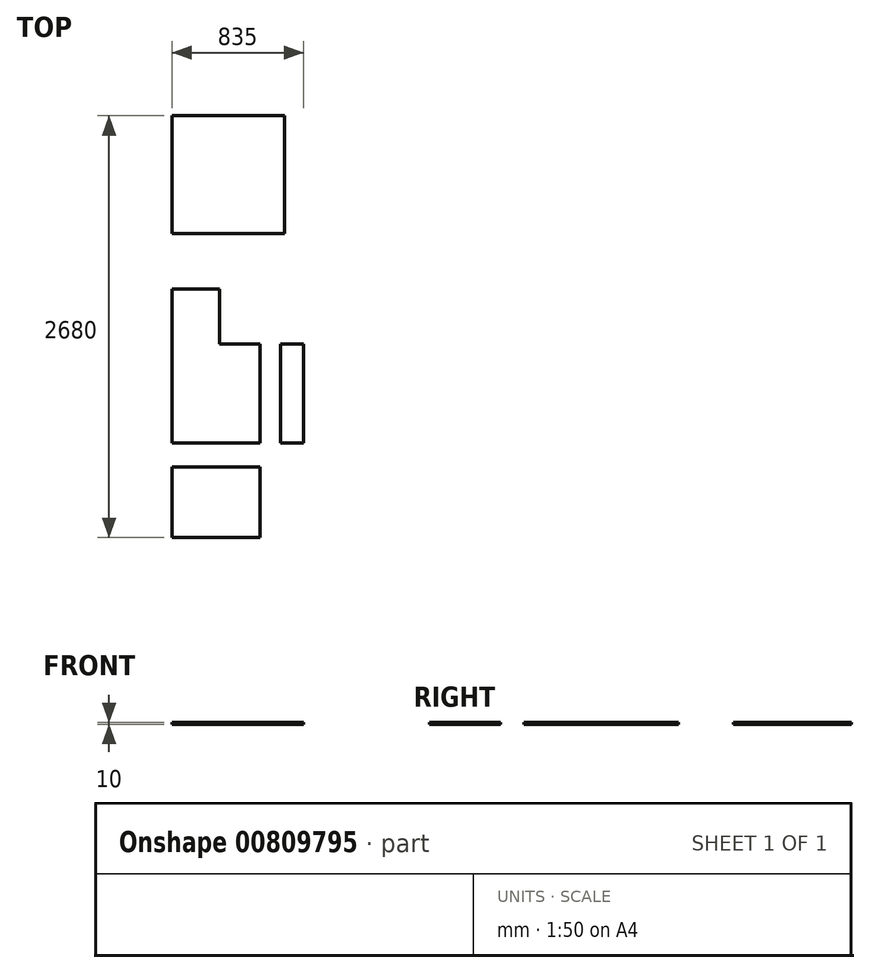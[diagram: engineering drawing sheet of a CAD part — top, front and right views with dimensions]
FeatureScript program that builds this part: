
annotation { "Feature Type Name" : "Feature", "Feature Type Description" : "" }
export const myFeature = defineFeature(function(context is Context, id is Id, definition is map)
    precondition{}
    {
        {
            var Q0;
            Q0=qCreatedBy(makeId("Top.planeOp"),FACE);
            var sketch = newSketch(context, id + "F0", { "sketchPlane" : qUnion([Q0])});
            skLineSegment(sketch, "E0.bottom", {"start": v(0, 0) * mm, "end": v(715, 0) * mm});
            skLineSegment(sketch, "E0.top", {"start": v(0, -750) * mm, "end": v(715, -750) * mm});
            skLineSegment(sketch, "E0.left", {"start": v(0, 0) * mm, "end": v(0, -750) * mm});
            skLineSegment(sketch, "E0.right", {"start": v(715, 0) * mm, "end": v(715, -750) * mm});
            skSolve(sketch);
        }
        {
            var Q0;
            Q0 = qSketchRegion(id + "F0", true);
            extrude(context, id + "F1", {"entities" : qUnion([Q0]), "depth" : 10 * mm, "offsetDistance" : 25 * mm});
        }
        {
            var Q0;
            Q0=qCreatedBy(makeId("Top.planeOp"),FACE);
            var sketch = newSketch(context, id + "F2", { "sketchPlane" : qUnion([Q0])});
            skLineSegment(sketch, "E1.bottom", {"start": v(0, -1100) * mm, "end": v(300, -1100) * mm});
            skLineSegment(sketch, "E1.top", {"start": v(0, -2080) * mm, "end": v(560, -2080) * mm});
            skLineSegment(sketch, "E1.left", {"start": v(0, -1100) * mm, "end": v(0, -2080) * mm});
            skLineSegment(sketch, "E1.right", {"start": v(560, -1450) * mm, "end": v(560, -2080) * mm});
            skLineSegment(sketch, "E2.top", {"start": v(300, -1450) * mm, "end": v(560, -1450) * mm});
            skLineSegment(sketch, "E2.left", {"start": v(300, -1100) * mm, "end": v(300, -1450) * mm});
            skSolve(sketch);
        }
        {
            var Q0;
            Q0=makeQuery(id+"F2.imprint","IMPRINT",FACE,{"disambiguationData":[TD([[makeQuery(id+"F2.imprint","IMPRINT",EDGE,{"derivedFrom":sQuery(id+"F2.wireOp",EDGE,"E1.bottom")}),-1.0]])]});
            extrude(context, id + "F3", {"entities" : qUnion([Q0]), "depth" : 10 * mm, "offsetDistance" : 25 * mm});
        }
        {
            var Q0;
            Q0=qCreatedBy(makeId("Top.planeOp"),FACE);
            var sketch = newSketch(context, id + "F4", { "sketchPlane" : qUnion([Q0])});
            skLineSegment(sketch, "E3.bottom", {"start": v(690, -1450) * mm, "end": v(835, -1450) * mm});
            skLineSegment(sketch, "E3.top", {"start": v(690, -2080) * mm, "end": v(835, -2080) * mm});
            skLineSegment(sketch, "E3.left", {"start": v(690, -1450) * mm, "end": v(690, -2080) * mm});
            skLineSegment(sketch, "E3.right", {"start": v(835, -1450) * mm, "end": v(835, -2080) * mm});
            skSolve(sketch);
        }
        {
            var Q0;
            Q0 = qSketchRegion(id + "F4", true);
            extrude(context, id + "F5", {"entities" : qUnion([Q0]), "depth" : 10 * mm, "offsetDistance" : 25 * mm});
        }
        {
            var Q0;
            Q0=qCreatedBy(makeId("Top.planeOp"),FACE);
            var sketch = newSketch(context, id + "F6", { "sketchPlane" : qUnion([Q0])});
            skLineSegment(sketch, "E4.bottom", {"start": v(0, -2230) * mm, "end": v(560, -2230) * mm});
            skLineSegment(sketch, "E4.top", {"start": v(0, -2680) * mm, "end": v(560, -2680) * mm});
            skLineSegment(sketch, "E4.left", {"start": v(0, -2230) * mm, "end": v(0, -2680) * mm});
            skLineSegment(sketch, "E4.right", {"start": v(560, -2230) * mm, "end": v(560, -2680) * mm});
            skSolve(sketch);
        }
        {
            var Q0;
            Q0=makeQuery(id+"F6.imprint","IMPRINT",FACE,{"disambiguationData":[TD([[makeQuery(id+"F6.imprint","IMPRINT",EDGE,{"derivedFrom":sQuery(id+"F6.wireOp",EDGE,"E4.bottom")}),-1.0]])]});
            extrude(context, id + "F7", {"entities" : qUnion([Q0]), "depth" : 10 * mm, "offsetDistance" : 25 * mm});
        }
    });
